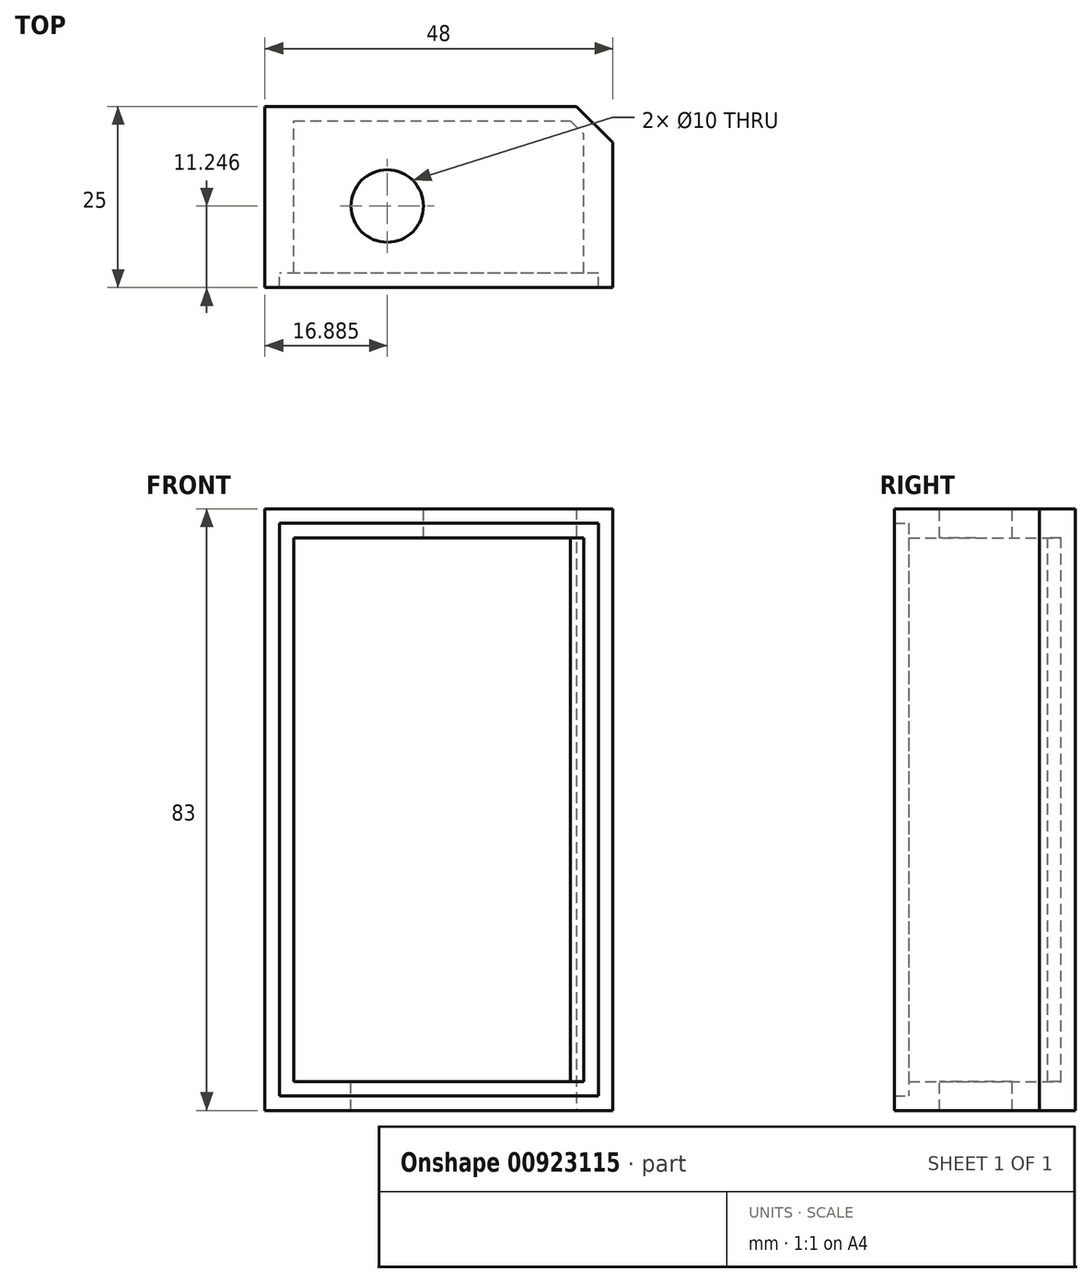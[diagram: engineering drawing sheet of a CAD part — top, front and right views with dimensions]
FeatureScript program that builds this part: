
annotation { "Feature Type Name" : "Feature", "Feature Type Description" : "" }
export const myFeature = defineFeature(function(context is Context, id is Id, definition is map)
    precondition{}
    {
        {
            var Q0;
            Q0=qCreatedBy(makeId("Front.planeOp"),FACE);
            var sketch = newSketch(context, id + "F0", { "sketchPlane" : qUnion([Q0])});
            skLineSegment(sketch, "E0.bottom", {"start": v(20, 37.5) * mm, "end": v(-20, 37.5) * mm});
            skLineSegment(sketch, "E0.top", {"start": v(20, -37.5) * mm, "end": v(-20, -37.5) * mm});
            skLineSegment(sketch, "E0.left", {"start": v(20, 37.5) * mm, "end": v(20, -37.5) * mm});
            skLineSegment(sketch, "E0.right", {"start": v(-20, 37.5) * mm, "end": v(-20, -37.5) * mm});
            skPoint(sketch, "E0.middle", {"position": v(0, 0) * mm});
            skLineSegment(sketch, "E1.bottom", {"start": v(22, 39.5) * mm, "end": v(-22, 39.5) * mm});
            skLineSegment(sketch, "E1.top", {"start": v(22, -39.5) * mm, "end": v(-22, -39.5) * mm});
            skLineSegment(sketch, "E1.left", {"start": v(22, 39.5) * mm, "end": v(22, -39.5) * mm});
            skLineSegment(sketch, "E1.right", {"start": v(-22, 39.5) * mm, "end": v(-22, -39.5) * mm});
            skLineSegment(sketch, "E2.bottom", {"start": v(24, 41.5) * mm, "end": v(-24, 41.5) * mm});
            skLineSegment(sketch, "E2.top", {"start": v(24, -41.5) * mm, "end": v(-24, -41.5) * mm});
            skLineSegment(sketch, "E2.left", {"start": v(24, 41.5) * mm, "end": v(24, -41.5) * mm});
            skLineSegment(sketch, "E2.right", {"start": v(-24, 41.5) * mm, "end": v(-24, -41.5) * mm});
            skSolve(sketch);
        }
        {
            var Q0;
            Q0=makeQuery(id+"F0.imprint","IMPRINT",FACE,{"disambiguationData":[TD([[makeQuery(id+"F0.imprint","IMPRINT",EDGE,{"derivedFrom":sQuery(id+"F0.wireOp",EDGE,"E0.bottom")}),1.0]])]});
            var Q1;
            Q1=makeQuery(id+"F0.imprint","IMPRINT",FACE,{"disambiguationData":[TD([[makeQuery(id+"F0.imprint","IMPRINT",EDGE,{"derivedFrom":sQuery(id+"F0.wireOp",EDGE,"E0.bottom")}),-1.0]])]});
            var Q2;
            Q2=makeQuery(id+"F0.imprint","IMPRINT",FACE,{"disambiguationData":[TD([[makeQuery(id+"F0.imprint","IMPRINT",EDGE,{"derivedFrom":sQuery(id+"F0.wireOp",EDGE,"E1.bottom")}),-1.0]])]});
            extrude(context, id + "F1", {"entities" : qUnion([Q0, Q1, Q2]), "depth" : 2 * mm, "offsetDistance" : 25 * mm});
        }
        {
            var Q0;
            Q0 = qSketchRegion(id + "F0", true);
            extrude(context, id + "F2", {"entities" : qUnion([Q0]), "operationType" : NewBodyOperationType.ADD, "depth" : 25 * mm, "offsetDistance" : 25 * mm});
        }
        {
            var Q0;
            Q0=makeQuery(id+"F0.imprint","IMPRINT",FACE,{"disambiguationData":[TD([[makeQuery(id+"F0.imprint","IMPRINT",EDGE,{"derivedFrom":sQuery(id+"F0.wireOp",EDGE,"E0.bottom")}),-1.0]])]});
            extrude(context, id + "F3", {"entities" : qUnion([Q0]), "operationType" : NewBodyOperationType.ADD, "depth" : 23 * mm, "offsetDistance" : 25 * mm});
        }
        {
            var Q0;
            Q0=makeQuery(id+"F1.opExtrude","CAP_EDGE",EDGE,{"disambiguationData":[OSD([sQuery(id+"F0.wireOp",EDGE,"E2.left")])],"isStart":true});
            chamfer(context, id + "F4", {"entities" : qUnion([Q0]), "chamferType" : ChamferType.OFFSET_ANGLE, "width" : 5 * mm, "oppositeDirection" : false, "angle" : 45 * degree, "tangentPropagation" : true});
        }
        {
            var Q0;
            Q0=qCreatedBy(makeId("Front.planeOp"),FACE);
            var sketch = newSketch(context, id + "F5", { "sketchPlane" : qUnion([Q0])});
            skSolve(sketch);
        }
        {
            var Q0;
            Q0 = qSketchRegion(id + "F5", true);
            var Q1;
            Q1=makeQuery(id+"F4.opChamfer","BLEND_FACE",FACE,{"disambiguationData":[OSD([sQuery(id+"F0.wireOp",EDGE,"E2.left")])]});
            extrude(context, id + "F6", {"entities" : qUnion([Q0, Q1]), "operationType" : NewBodyOperationType.ADD, "oppositeDirection" : true, "depth" : 2 * mm, "offsetDistance" : 25 * mm});
        }
        {
            var Q0;
            {var subQ0=sQuery(id+"F0.wireOp",EDGE,"E2.bottom");Q0=makeQuery(id+"F2.boolean.opBoolean","MERGE",FACE,{"derivedFrom":[makeQuery(id+"F1.opExtrude","SWEPT_FACE",FACE,{"disambiguationData":[OSD([subQ0])]}),makeQuery(id+"F2.opExtrude","SWEPT_FACE",FACE,{"disambiguationData":[OSD([subQ0])]})]});}
            var sketch = newSketch(context, id + "F7", { "sketchPlane" : qUnion([Q0])});
            skSolve(sketch);
        }
        {
            var Q0;
            {var subQ0=sQuery(id+"F0.wireOp",EDGE,"E2.bottom");Q0=makeQuery(id+"F7.imprint","IMPRINT",FACE,{"disambiguationData":[TD([[makeQuery(id+"F7.imprint","IMPRINT",EDGE,{"derivedFrom":makeQuery(id+"F2.opExtrude","CAP_EDGE",EDGE,{"disambiguationData":[OSD([subQ0])],"isStart":false})}),-1.0]])]});}
            var sketch = newSketch(context, id + "F8", { "sketchPlane" : qUnion([Q0])});
            skSolve(sketch);
        }
        {
            var Q0;
            {var subQ0=sQuery(id+"F0.wireOp",EDGE,"E2.bottom");Q0=makeQuery(id+"F8.imprint","IMPRINT",FACE,{"disambiguationData":[TD([[makeQuery(id+"F8.imprint","IMPRINT",EDGE,{"derivedFrom":makeQuery(id+"F7.imprint","IMPRINT",EDGE,{"derivedFrom":makeQuery(id+"F2.opExtrude","CAP_EDGE",EDGE,{"disambiguationData":[OSD([subQ0])],"isStart":false})})}),-1.0]])]});}
            var sketch = newSketch(context, id + "F9", { "sketchPlane" : qUnion([Q0])});
            skSolve(sketch);
        }
        {
            var Q0;
            {var subQ0=sQuery(id+"F0.wireOp",EDGE,"E2.bottom");Q0=makeQuery(id+"F9.imprint","IMPRINT",FACE,{"disambiguationData":[TD([[makeQuery(id+"F9.imprint","IMPRINT",EDGE,{"derivedFrom":makeQuery(id+"F8.imprint","IMPRINT",EDGE,{"derivedFrom":makeQuery(id+"F7.imprint","IMPRINT",EDGE,{"derivedFrom":makeQuery(id+"F2.opExtrude","CAP_EDGE",EDGE,{"disambiguationData":[OSD([subQ0])],"isStart":false})})})}),-1.0]])]});}
            var sketch = newSketch(context, id + "F10", { "sketchPlane" : qUnion([Q0])});
            skLineSegment(sketch, "E3", {"start": v(0, 0) * mm, "end": v(0, 0) * mm});
            skLineSegment(sketch, "E4", {"start": v(0, 0) * mm, "end": v(0, -25) * mm});
            skLineSegment(sketch, "E5", {"start": v(0, -25) * mm, "end": v(-15.37, -25) * mm});
            skLineSegment(sketch, "E6", {"start": v(-15.37, -25) * mm, "end": v(-15.37, 0) * mm});
            skLineSegment(sketch, "E7", {"start": v(-15.37, 0) * mm, "end": v(0, 0) * mm});
            skSolve(sketch);
        }
        {
            var Q0;
            {var subQ0=sQuery(id+"F10.wireOp",EDGE,"E7");Q0=makeQuery(id+"F10.imprint","IMPRINT",FACE,{"disambiguationData":[TD([[makeQuery(id+"F10.imprint","IMPRINT",EDGE,{"derivedFrom":subQ0}),1.0]])]});}
            var sketch = newSketch(context, id + "F11", { "sketchPlane" : qUnion([Q0])});
            skPoint(sketch, "E8", {"position": v(-7.11, -13.75) * mm});
            skPoint(sketch, "E9", {"position": v(-23.93, -13.75) * mm});
            skPoint(sketch, "E10", {"position": v(-7.11, 0.1) * mm});
            skSolve(sketch);
        }
        {
            var Q0;
            Q0=sQuery(id+"F11.wireOp",VERTEX,"E8");
            var Q1;
            Q1=makeQuery(id+"F1.opExtrude","SWEPT_BODY",BODY,{"disambiguationData":[OSD([sQuery(id+"F0.wireOp",EDGE,"E2.bottom"),sQuery(id+"F0.wireOp",EDGE,"E2.top"),sQuery(id+"F0.wireOp",EDGE,"E2.left"),sQuery(id+"F0.wireOp",EDGE,"E2.right")])]});
            hole(context, id + "F12", {"style" : HoleStyle.SIMPLE, "endStyle" : HoleEndStyle.THROUGH, "holeDiameter" : 10 * mm, "majorDiameter" : 5 * mm, "isTappedThrough" : true, "tappedDepth" : 12 * mm, "tapClearance" : 3, "locations" : qUnion([Q0]), "scope" : qUnion([Q1])});
        }
    });
